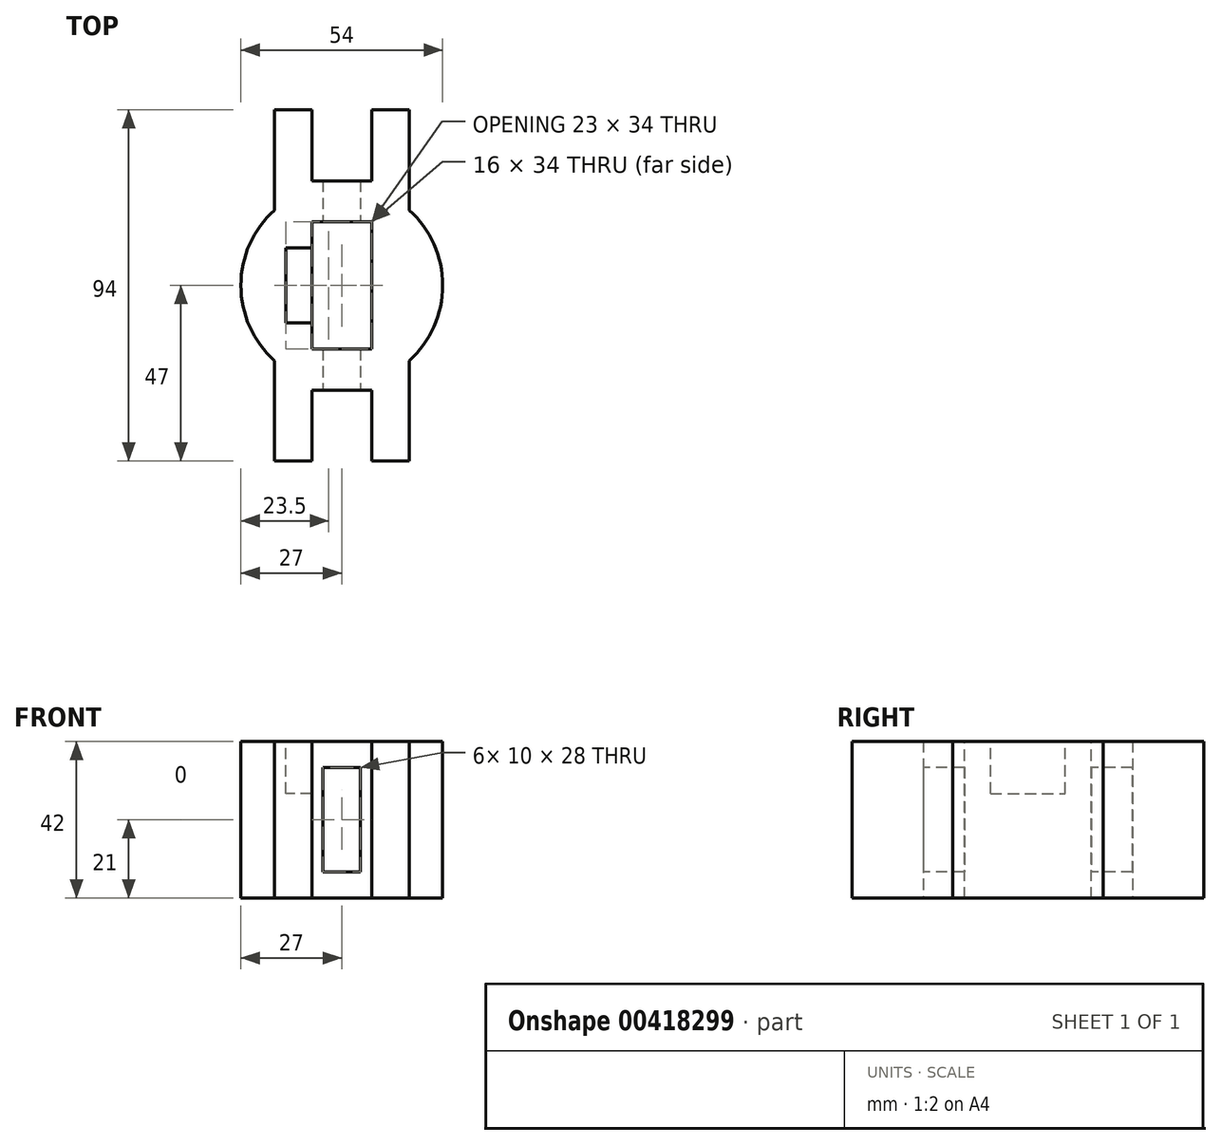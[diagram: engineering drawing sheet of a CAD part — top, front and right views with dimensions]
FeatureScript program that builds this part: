
annotation { "Feature Type Name" : "Feature", "Feature Type Description" : "" }
export const myFeature = defineFeature(function(context is Context, id is Id, definition is map)
    precondition{}
    {
        {
            var Q0;
            Q0=qCreatedBy(makeId("Top.planeOp"),FACE);
            var sketch = newSketch(context, id + "F0", { "sketchPlane" : qUnion([Q0])});
            skLineSegment(sketch, "E0.bottom", {"start": v(-27, 47) * mm, "end": v(27, 47) * mm, "construction": true});
            skLineSegment(sketch, "E0.top", {"start": v(-27, -47) * mm, "end": v(27, -47) * mm, "construction": true});
            skLineSegment(sketch, "E0.left", {"start": v(-27, 47) * mm, "end": v(-27, -47) * mm, "construction": true});
            skLineSegment(sketch, "E0.right", {"start": v(27, 47) * mm, "end": v(27, -47) * mm, "construction": true});
            skPoint(sketch, "E0.middle", {"position": v(0, 0) * mm});
            skLineSegment(sketch, "E1", {"start": v(0, 47) * mm, "end": v(0, -47) * mm, "construction": true});
            skLineSegment(sketch, "E2", {"start": v(0, -28) * mm, "end": v(-8, -28) * mm});
            skLineSegment(sketch, "E3", {"start": v(-8, -28) * mm, "end": v(-8, -47) * mm});
            skLineSegment(sketch, "E4", {"start": v(-8, -47) * mm, "end": v(-18, -47) * mm});
            skLineSegment(sketch, "E5", {"start": v(-18, -47) * mm, "end": v(-18, -20.12) * mm});
            skArc(sketch, "E6.trimOffspring", {"start": v(-27, 0) * mm, "mid": v(-24.65, -11.02) * mm, "end": v(-18, -20.12) * mm});
            skArc(sketch, "E7.MirrorCS", {"start": v(27, 0) * mm, "mid": v(24.65, -11.02) * mm, "end": v(18, -20.12) * mm});
            skLineSegment(sketch, "E8.MirrorCS", {"start": v(18, -47) * mm, "end": v(18, -20.12) * mm});
            skLineSegment(sketch, "E9.MirrorCS", {"start": v(8, -47) * mm, "end": v(18, -47) * mm});
            skLineSegment(sketch, "E10.MirrorCS", {"start": v(8, -28) * mm, "end": v(8, -47) * mm});
            skLineSegment(sketch, "E11.MirrorCS", {"start": v(0, -28) * mm, "end": v(8, -28) * mm});
            skArc(sketch, "E12.MirrorCS", {"start": v(-27, 0) * mm, "mid": v(-24.65, 11.02) * mm, "end": v(-18, 20.12) * mm});
            skLineSegment(sketch, "E13.MirrorCS", {"start": v(-18, 47) * mm, "end": v(-18, 20.12) * mm});
            skLineSegment(sketch, "E14.MirrorCS", {"start": v(0, 28) * mm, "end": v(8, 28) * mm});
            skLineSegment(sketch, "E15.MirrorCS", {"start": v(8, 28) * mm, "end": v(8, 47) * mm});
            skLineSegment(sketch, "E16.MirrorCS", {"start": v(8, 47) * mm, "end": v(18, 47) * mm});
            skLineSegment(sketch, "E17.MirrorCS", {"start": v(-8, 47) * mm, "end": v(-18, 47) * mm});
            skLineSegment(sketch, "E18.MirrorCS", {"start": v(0, 28) * mm, "end": v(-8, 28) * mm});
            skLineSegment(sketch, "E19.MirrorCS", {"start": v(-8, 28) * mm, "end": v(-8, 47) * mm});
            skArc(sketch, "E20.MirrorCS", {"start": v(27, 0) * mm, "mid": v(24.65, 11.02) * mm, "end": v(18, 20.12) * mm});
            skLineSegment(sketch, "E21", {"start": v(18, 47) * mm, "end": v(18, 20.12) * mm});
            skSolve(sketch);
        }
        {
            var Q0;
            Q0 = qSketchRegion(id + "F0", true);
            extrude(context, id + "F1", {"entities" : qUnion([Q0]), "endBound" : BoundingType.SYMMETRIC, "depth" : 42 * mm});
        }
        {
            var Q0;
            Q0=makeQuery(id+"F1.opExtrude","SWEPT_FACE",FACE,{"disambiguationData":[OSD([sQuery(id+"F0.wireOp",EDGE,"E2"),sQuery(id+"F0.wireOp",EDGE,"E11.MirrorCS")])]});
            var sketch = newSketch(context, id + "F2", { "sketchPlane" : qUnion([Q0])});
            skLineSegment(sketch, "E22.bottom", {"start": v(5, 14) * mm, "end": v(-5, 14) * mm});
            skLineSegment(sketch, "E22.top", {"start": v(5, -14) * mm, "end": v(-5, -14) * mm});
            skLineSegment(sketch, "E22.left", {"start": v(5, 14) * mm, "end": v(5, -14) * mm});
            skLineSegment(sketch, "E22.right", {"start": v(-5, 14) * mm, "end": v(-5, -14) * mm});
            skPoint(sketch, "E22.middle", {"position": v(0, 0) * mm});
            skSolve(sketch);
        }
        {
            var Q0;
            Q0 = qSketchRegion(id + "F2", true);
            extrude(context, id + "F3", {"entities" : qUnion([Q0]), "operationType" : NewBodyOperationType.REMOVE, "endBound" : BoundingType.THROUGH_ALL, "oppositeDirection" : true, "depth" : 25 * mm});
        }
        {
            var Q0;
            Q0=makeQuery(id+"F1.opExtrude","CAP_FACE",FACE,{"disambiguationData":[OSD([sQuery(id+"F0.wireOp",EDGE,"E2"),sQuery(id+"F0.wireOp",EDGE,"E3"),sQuery(id+"F0.wireOp",EDGE,"E4"),sQuery(id+"F0.wireOp",EDGE,"E5"),sQuery(id+"F0.wireOp",EDGE,"E6.trimOffspring"),sQuery(id+"F0.wireOp",EDGE,"E7.MirrorCS"),sQuery(id+"F0.wireOp",EDGE,"E8.MirrorCS"),sQuery(id+"F0.wireOp",EDGE,"E9.MirrorCS"),sQuery(id+"F0.wireOp",EDGE,"E10.MirrorCS"),sQuery(id+"F0.wireOp",EDGE,"E11.MirrorCS"),sQuery(id+"F0.wireOp",EDGE,"E12.MirrorCS"),sQuery(id+"F0.wireOp",EDGE,"E14.MirrorCS"),sQuery(id+"F0.wireOp",EDGE,"E16.MirrorCS"),sQuery(id+"F0.wireOp",EDGE,"E13.MirrorCS"),sQuery(id+"F0.wireOp",EDGE,"E17.MirrorCS"),sQuery(id+"F0.wireOp",EDGE,"E18.MirrorCS"),sQuery(id+"F0.wireOp",EDGE,"E19.MirrorCS"),sQuery(id+"F0.wireOp",EDGE,"E20.MirrorCS"),sQuery(id+"F0.wireOp",EDGE,"E15.MirrorCS"),sQuery(id+"F0.wireOp",EDGE,"E21")])],"isStart":false});
            var sketch = newSketch(context, id + "F4", { "sketchPlane" : qUnion([Q0])});
            skLineSegment(sketch, "E23.bottom", {"start": v(8, -17) * mm, "end": v(-8, -17) * mm});
            skLineSegment(sketch, "E23.top", {"start": v(8, 17) * mm, "end": v(-8, 17) * mm});
            skLineSegment(sketch, "E23.left", {"start": v(8, -17) * mm, "end": v(8, 17) * mm});
            skLineSegment(sketch, "E23.right", {"start": v(-8, -17) * mm, "end": v(-8, 17) * mm});
            skPoint(sketch, "E23.middle", {"position": v(0, 0) * mm});
            skSolve(sketch);
        }
        {
            var Q0;
            Q0 = qSketchRegion(id + "F4", true);
            extrude(context, id + "F5", {"entities" : qUnion([Q0]), "operationType" : NewBodyOperationType.REMOVE, "endBound" : BoundingType.THROUGH_ALL, "oppositeDirection" : true, "depth" : 25 * mm});
        }
        {
            var Q0;
            Q0=makeQuery(id+"F1.opExtrude","CAP_FACE",FACE,{"disambiguationData":[OSD([sQuery(id+"F0.wireOp",EDGE,"E2"),sQuery(id+"F0.wireOp",EDGE,"E3"),sQuery(id+"F0.wireOp",EDGE,"E4"),sQuery(id+"F0.wireOp",EDGE,"E5"),sQuery(id+"F0.wireOp",EDGE,"E6.trimOffspring"),sQuery(id+"F0.wireOp",EDGE,"E7.MirrorCS"),sQuery(id+"F0.wireOp",EDGE,"E8.MirrorCS"),sQuery(id+"F0.wireOp",EDGE,"E9.MirrorCS"),sQuery(id+"F0.wireOp",EDGE,"E10.MirrorCS"),sQuery(id+"F0.wireOp",EDGE,"E11.MirrorCS"),sQuery(id+"F0.wireOp",EDGE,"E12.MirrorCS"),sQuery(id+"F0.wireOp",EDGE,"E14.MirrorCS"),sQuery(id+"F0.wireOp",EDGE,"E16.MirrorCS"),sQuery(id+"F0.wireOp",EDGE,"E13.MirrorCS"),sQuery(id+"F0.wireOp",EDGE,"E17.MirrorCS"),sQuery(id+"F0.wireOp",EDGE,"E18.MirrorCS"),sQuery(id+"F0.wireOp",EDGE,"E19.MirrorCS"),sQuery(id+"F0.wireOp",EDGE,"E20.MirrorCS"),sQuery(id+"F0.wireOp",EDGE,"E15.MirrorCS"),sQuery(id+"F0.wireOp",EDGE,"E21")])],"isStart":false});
            var sketch = newSketch(context, id + "F6", { "sketchPlane" : qUnion([Q0])});
            skLineSegment(sketch, "E24.bottom", {"start": v(-8, 10) * mm, "end": v(-15, 10) * mm});
            skLineSegment(sketch, "E24.top", {"start": v(-8, -10) * mm, "end": v(-15, -10) * mm});
            skLineSegment(sketch, "E24.left", {"start": v(-8, 10) * mm, "end": v(-8, -10) * mm});
            skLineSegment(sketch, "E24.right", {"start": v(-15, 10) * mm, "end": v(-15, -10) * mm});
            skSolve(sketch);
        }
        {
            var Q0;
            Q0 = qSketchRegion(id + "F6", true);
            extrude(context, id + "F7", {"entities" : qUnion([Q0]), "operationType" : NewBodyOperationType.REMOVE, "oppositeDirection" : true, "depth" : 14 * mm});
        }
    });
